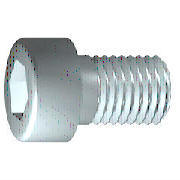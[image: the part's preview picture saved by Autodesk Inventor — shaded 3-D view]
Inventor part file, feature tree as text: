
AUTODESK INVENTOR PART (.ipt)
format: ipt  version: 2016 (Build 200138000, 138)  size: 193,536 bytes
history: native  units: mm (DEFAULTED — no unit token found)
features: sketch x2, extrude x1, plane x1, fillet x1
ambient origin geometry x7: Origin, YZ Plane, XY Plane, X Axis, Y Axis, Z Axis, Center Point
bodies: Solid1 (feature_tree), Body (feature_tree)
feature tree (5):
  extrude  "Slot"  Depth=2.5mm
  plane  "Work Plane1"
  fillet  "Fillet2"  Radius=2.5mm
  sketch  "Sketch1"  dims[d1=4.875mm d2=0.276153mm d3=2.5mm]
  sketch  "Sketch2"  dims[d4=1.1mm d5=60.0deg d6=2.5mm d7=2.5mm d8=2.309401mm d9=4.5mm d10=90.0deg d11=10.0mm d12=0.0mm d13=4.875mm d14=0.0mm d15=0.276052mm d16=0.276053mm d17=0.25mm d19=0.0mm d26=6.0mm d27=45.0deg d28=0.0mm d29=0.0mm d30=0.1mm]
